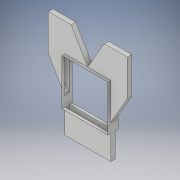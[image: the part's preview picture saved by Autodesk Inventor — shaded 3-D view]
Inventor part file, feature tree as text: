
AUTODESK INVENTOR PART (.ipt)
format: ipt  version: 2017 (Build 210142000, 142)  size: 263,680 bytes
history: native  units: in
note: dims shown in document units (in); Inventor stores cm internally (conversion verified against a paired STEP export)
features: extrude x6, sketch x6, other x3, delete_face x1
ambient origin geometry x8: Origin, YZ Plane, XZ Plane, XY Plane, X Axis, Y Axis, Z Axis, Center Point
bodies: Body1 (feature_tree)
feature tree (16):
  other  "rame of door"
  extrude  "frame"  Depth=100.0in
  other  "middle of part"
  extrude  "door slot bottom"  Depth=10.0in
  extrude  "top left and right slots"  Depth=10.0in
  extrude  "door recieves"  Depth=0.7071in
  extrude  "front hide door"  Depth=10.0in TaperAngle=0.0deg
  extrude  "gap for door pieces"  Depth=2.0in
  other  "mate for door pieces"
  delete_face  "Delete Face1"
  sketch  "Sketch1"  dims[d0=100.0in d1=100.0in]
  sketch  "Sketch7"  dims[d3=10.0in d4=10.0in]
  sketch  "Sketch8"  dims[d5=10.0in d6=10.0in]
  sketch  "Sketch13"  dims[d7=22.0in d8=0.0in d118=0.7071in d178=0.8316in]
  sketch  "Sketch14"  dims[d459=10.0in d460=0.0in d865=10.0in d866=0.0in]
  sketch  "Sketch15"  dims[d878=60.0deg d889=2.0in d901=2.0in d903=51.0in d907=10.0in d916=10.0in d917=10.0in d919=10.0in d920=10.0in d921=10.0in d922=22.0in d923=0.0in d926=25.7957in d927=52.0in d928=21.0in d929=0.0in d930=10.0in d931=0.0in d932=50.0in]
